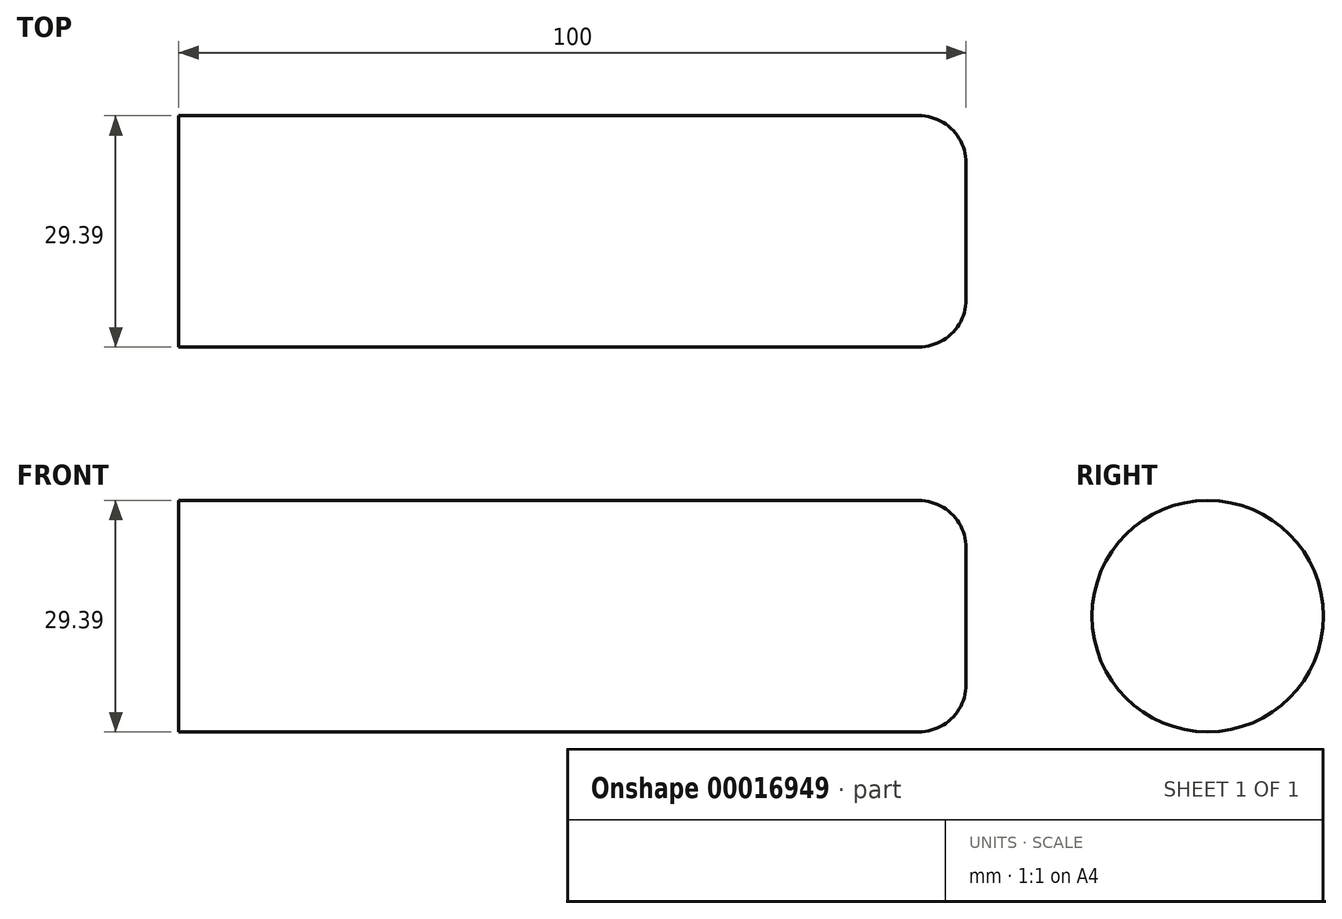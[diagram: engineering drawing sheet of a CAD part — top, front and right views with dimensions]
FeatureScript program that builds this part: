
annotation { "Feature Type Name" : "Feature", "Feature Type Description" : "" }
export const myFeature = defineFeature(function(context is Context, id is Id, definition is map)
    precondition{}
    {
        {
            var Q0;
            Q0=qCreatedBy(makeId("Right.planeOp"),FACE);
            var sketch = newSketch(context, id + "F0", { "sketchPlane" : qUnion([Q0])});
            skCircle(sketch, "E0", {"center": v(-59.6, 29.63) * mm, "radius": 14.7 * mm});
            skSolve(sketch);
        }
        {
            var Q0;
            Q0=makeQuery(id+"F0.imprint","IMPRINT",FACE,{"disambiguationData":[TD([[makeQuery(id+"F0.imprint","IMPRINT",EDGE,{"derivedFrom":sQuery(id+"F0.wireOp",EDGE,"E0")}),1.0]])]});
            extrude(context, id + "F1", {"entities" : qUnion([Q0]), "oppositeDirection" : true, "depth" : 100 * mm});
        }
        {
            var Q0;
            Q0=makeQuery(id+"F1.opExtrude","CAP_EDGE",EDGE,{"disambiguationData":[OSD([sQuery(id+"F0.wireOp",EDGE,"E0")])],"isStart":true});
            fillet(context, id + "F2", {"entities" : qUnion([Q0]), "radius" : 6 * mm, "tangentPropagation" : true, "allowEdgeOverflow" : false});
        }
    });
